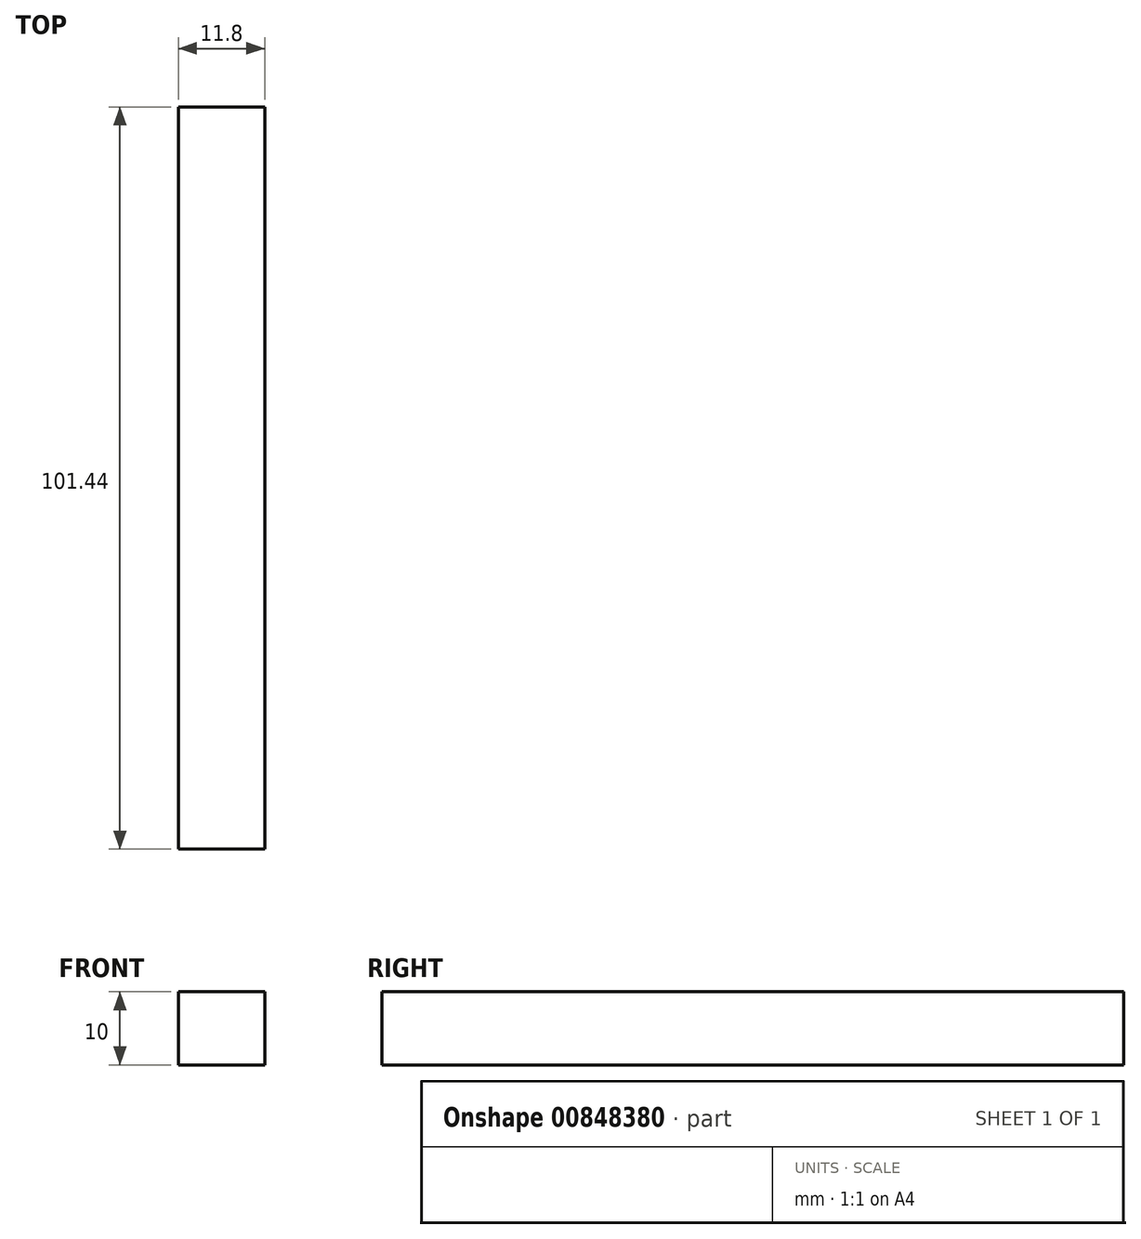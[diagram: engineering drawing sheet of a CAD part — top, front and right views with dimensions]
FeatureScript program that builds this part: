
annotation { "Feature Type Name" : "Feature", "Feature Type Description" : "" }
export const myFeature = defineFeature(function(context is Context, id is Id, definition is map)
    precondition{}
    {
        {
            var Q0;
            Q0=qCreatedBy(makeId("Top.planeOp"),FACE);
            var sketch = newSketch(context, id + "F0", { "sketchPlane" : qUnion([Q0])});
            skLineSegment(sketch, "E0.bottom", {"start": v(5.9, 50.72) * mm, "end": v(-5.9, 50.72) * mm});
            skLineSegment(sketch, "E0.top", {"start": v(5.9, -50.72) * mm, "end": v(-5.9, -50.72) * mm});
            skLineSegment(sketch, "E0.left", {"start": v(5.9, 50.72) * mm, "end": v(5.9, -50.72) * mm});
            skLineSegment(sketch, "E0.right", {"start": v(-5.9, 50.72) * mm, "end": v(-5.9, -50.72) * mm});
            skPoint(sketch, "E0.middle", {"position": v(0, 0) * mm});
            skSolve(sketch);
        }
        {
            var Q0;
            Q0 = qSketchRegion(id + "F0", true);
            extrude(context, id + "F1", {"entities" : qUnion([Q0]), "endBound" : BoundingType.SYMMETRIC, "depth" : 10 * mm, "offsetDistance" : 25 * mm});
        }
    });
